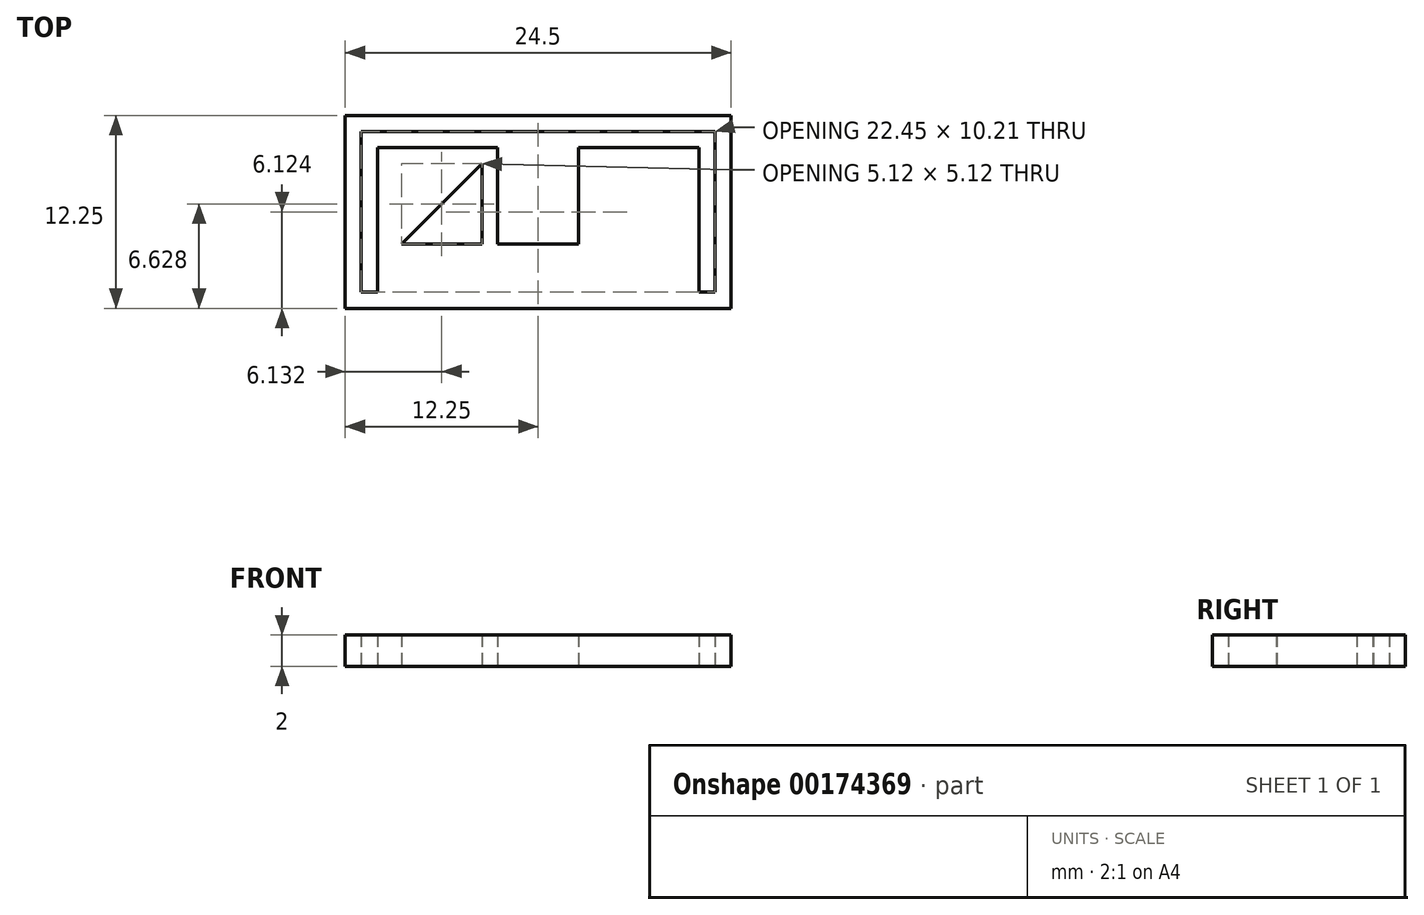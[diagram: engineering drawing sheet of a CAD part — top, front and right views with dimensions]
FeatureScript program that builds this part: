
annotation { "Feature Type Name" : "Feature", "Feature Type Description" : "" }
export const myFeature = defineFeature(function(context is Context, id is Id, definition is map)
    precondition{}
    {
        {
            var Q0;
            Q0=qCreatedBy(makeId("Top.planeOp"),FACE);
            var sketch = newSketch(context, id + "F0", { "sketchPlane" : qUnion([Q0])});
            skLineSegment(sketch, "E0.bottom", {"start": v(0, 0) * mm, "end": v(12.25, 0) * mm});
            skLineSegment(sketch, "E0.top", {"start": v(0, 12.25) * mm, "end": v(12.25, 12.25) * mm});
            skLineSegment(sketch, "E0.right", {"start": v(12.25, 0) * mm, "end": v(12.25, 12.25) * mm});
            skLineSegment(sketch, "E1.bottom", {"start": v(0, 0) * mm, "end": v(11.23, 0) * mm});
            skLineSegment(sketch, "E1.top", {"start": v(0, 11.23) * mm, "end": v(11.23, 11.23) * mm});
            skLineSegment(sketch, "E2.bottom", {"start": v(0, 0) * mm, "end": v(10.2, 0) * mm});
            skLineSegment(sketch, "E3", {"start": v(11.23, 1.02) * mm, "end": v(10.2, 1.02) * mm});
            skLineSegment(sketch, "E4.top", {"start": v(0, 4.1) * mm, "end": v(2.56, 4.1) * mm});
            skLineSegment(sketch, "E4.right", {"start": v(2.56, 10.22) * mm, "end": v(2.56, 4.1) * mm});
            skLineSegment(sketch, "E5", {"start": v(2.56, 10.22) * mm, "end": v(10.2, 10.2) * mm});
            skLineSegment(sketch, "E6", {"start": v(10.2, 10.2) * mm, "end": v(10.2, 1.02) * mm});
            skLineSegment(sketch, "E7", {"start": v(11.23, 11.23) * mm, "end": v(11.23, 1.02) * mm});
            skLineSegment(sketch, "E8.MirrorCS", {"start": v(-2.56, 10.22) * mm, "end": v(-2.56, 4.07) * mm});
            skLineSegment(sketch, "E9.MirrorCS", {"start": v(-12.25, 0) * mm, "end": v(-12.25, 12.25) * mm});
            skLineSegment(sketch, "E10.MirrorCS", {"start": v(0, 0) * mm, "end": v(-11.23, 0) * mm});
            skLineSegment(sketch, "E11.MirrorCS", {"start": v(0, 12.25) * mm, "end": v(-12.25, 12.25) * mm});
            skLineSegment(sketch, "E12.MirrorCS", {"start": v(-11.23, 1.02) * mm, "end": v(-10.2, 1.02) * mm});
            skLineSegment(sketch, "E13.MirrorCS", {"start": v(-2.56, 10.22) * mm, "end": v(-10.2, 10.2) * mm});
            skLineSegment(sketch, "E14.MirrorCS", {"start": v(0, 11.23) * mm, "end": v(-11.23, 11.23) * mm});
            skLineSegment(sketch, "E15.MirrorCS", {"start": v(-11.23, 11.23) * mm, "end": v(-11.23, 1.02) * mm});
            skLineSegment(sketch, "E16.MirrorCS", {"start": v(0, 0) * mm, "end": v(-12.25, 0) * mm});
            skLineSegment(sketch, "E17.MirrorCS", {"start": v(0, 4.1) * mm, "end": v(-2.56, 4.07) * mm});
            skLineSegment(sketch, "E18.MirrorCS", {"start": v(-10.2, 10.2) * mm, "end": v(-10.2, 1.02) * mm});
            skLineSegment(sketch, "E19.MirrorCS", {"start": v(0, 0) * mm, "end": v(-10.2, 0) * mm});
            skLineSegment(sketch, "E20", {"start": v(-3.56, 4.07) * mm, "end": v(-3.56, 9.19) * mm});
            skLineSegment(sketch, "E21", {"start": v(-3.56, 9.19) * mm, "end": v(-8.68, 4.07) * mm});
            skLineSegment(sketch, "E22", {"start": v(-8.68, 4.07) * mm, "end": v(-3.56, 4.07) * mm});
            skLineSegment(sketch, "E23", {"start": v(12.25, 0) * mm, "end": v(-12.25, 0) * mm});
            skLineSegment(sketch, "E24", {"start": v(-12.25, 12.25) * mm, "end": v(12.25, 12.25) * mm});
            skLineSegment(sketch, "E25", {"start": v(11.23, 11.23) * mm, "end": v(-11.23, 11.23) * mm});
            skLineSegment(sketch, "E26", {"start": v(2.56, 4.1) * mm, "end": v(-2.56, 4.07) * mm});
            skSolve(sketch);
        }
        {
            var Q0;
            {var subQ1=sQuery(id+"F0.wireOp",EDGE,"E0.right");Q0=makeQuery(id+"F0.imprint","IMPRINT",FACE,{"disambiguationData":[TD([[makeQuery(id+"F0.imprint","IMPRINT",EDGE,{"derivedFrom":subQ1}),1.0]])]});}
            extrude(context, id + "F1", {"entities" : qUnion([Q0]), "depth" : 2 * mm});
        }
    });
